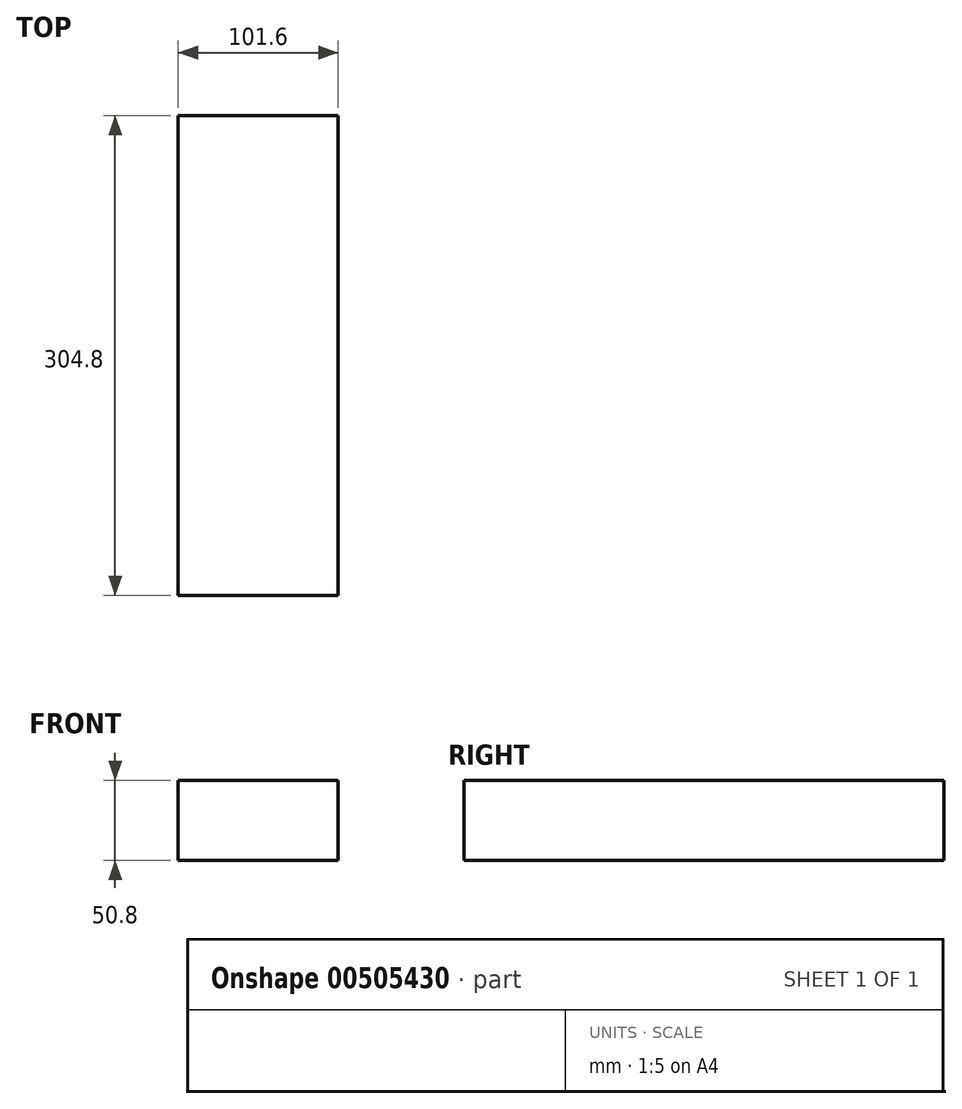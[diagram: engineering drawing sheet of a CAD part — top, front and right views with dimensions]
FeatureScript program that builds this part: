
annotation { "Feature Type Name" : "Feature", "Feature Type Description" : "" }
export const myFeature = defineFeature(function(context is Context, id is Id, definition is map)
    precondition{}
    {
        {
            var Q0;
            Q0=qCreatedBy(makeId("Top.planeOp"),FACE);
            var sketch = newSketch(context, id + "F0", { "sketchPlane" : qUnion([Q0])});
            skLineSegment(sketch, "E0", {"start": v(0, 304.8) * mm, "end": v(-50.8, 304.8) * mm});
            skLineSegment(sketch, "E1", {"start": v(0, 304.8) * mm, "end": v(50.8, 304.8) * mm});
            skLineSegment(sketch, "E2", {"start": v(-50.8, 304.8) * mm, "end": v(-50.8, 0) * mm});
            skLineSegment(sketch, "E3", {"start": v(50.8, 304.8) * mm, "end": v(50.8, 0) * mm});
            skLineSegment(sketch, "E4", {"start": v(-50.8, 0) * mm, "end": v(50.8, 0) * mm});
            skSolve(sketch);
        }
        {
            var Q0;
            Q0 = qSketchRegion(id + "F0", true);
            extrude(context, id + "F1", {"entities" : qUnion([Q0]), "depth" : 50.8 * mm});
        }
    });
